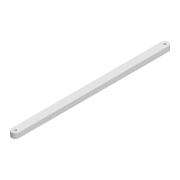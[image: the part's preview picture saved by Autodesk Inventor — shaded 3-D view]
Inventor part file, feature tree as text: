
AUTODESK INVENTOR PART (.ipt)
format: ipt  version: 2022 (Build 260153000, 153)  size: 90,112 bytes
history: native  units: mm
features: extrude x1, sketch x1
ambient origin geometry x8: Origin, YZ Plane, XZ Plane, XY Plane, X Axis, Y Axis, Z Axis, Center Point
bodies: Solid1 (feature_tree)
feature tree (2):
  extrude  "Extrusion1"  Depth=4.0mm
  sketch  "Sketch1"  dims[d0=2.2mm d1=2.2mm d2=6.0mm d3=120.239mm d6=4.0mm d7=0.0mm]
